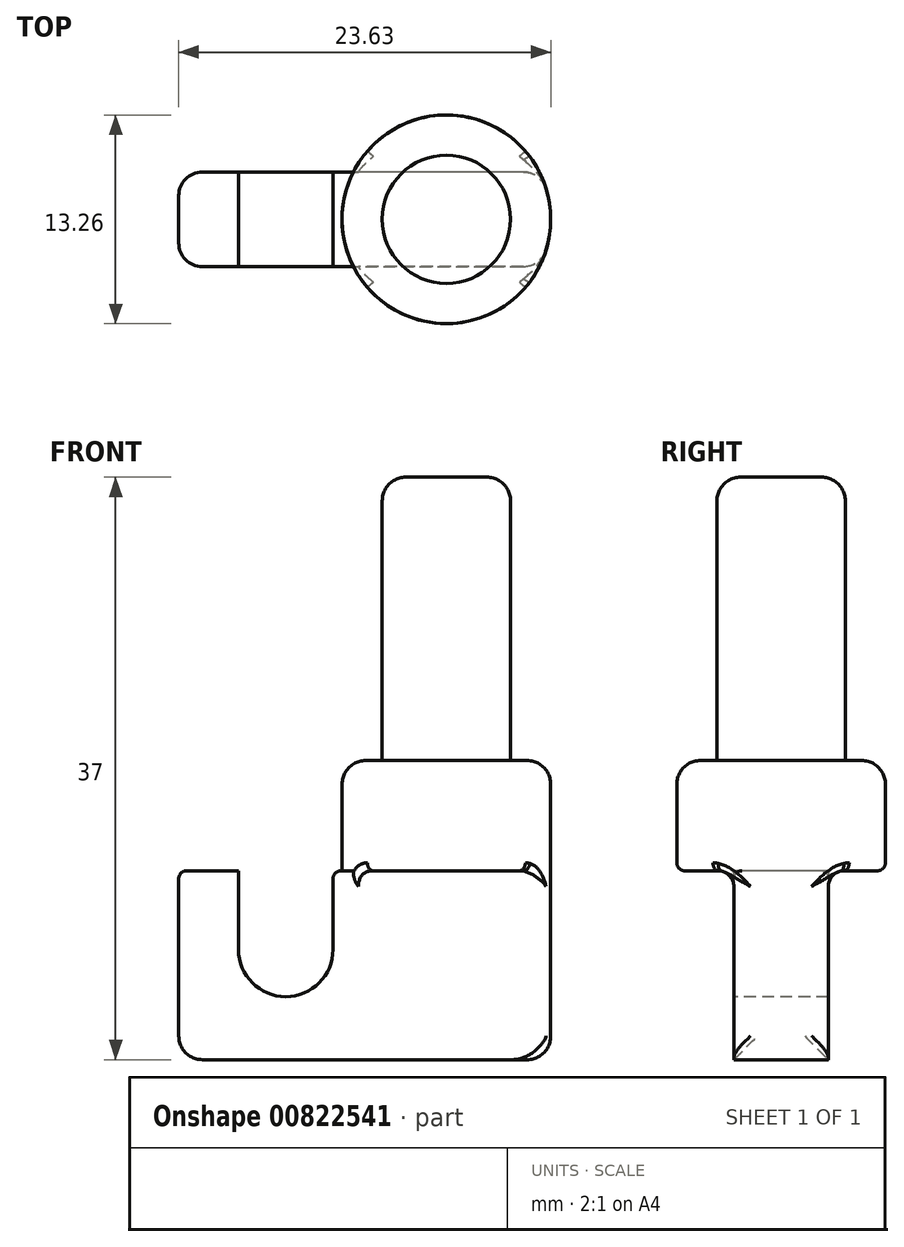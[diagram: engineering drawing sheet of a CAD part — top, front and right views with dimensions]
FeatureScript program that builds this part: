
annotation { "Feature Type Name" : "Feature", "Feature Type Description" : "" }
export const myFeature = defineFeature(function(context is Context, id is Id, definition is map)
    precondition{}
    {
        {
            var Q0;
            Q0=qCreatedBy(makeId("Top.planeOp"),FACE);
            var sketch = newSketch(context, id + "F0", { "sketchPlane" : qUnion([Q0])});
            skCircle(sketch, "E0", {"center": v(0, 0) * mm, "radius": 4.08 * mm});
            skCircle(sketch, "E1", {"center": v(0, 0) * mm, "radius": 6.62 * mm});
            skLineSegment(sketch, "E2", {"start": v(0, 0) * mm, "end": v(0, 3) * mm});
            skLineSegment(sketch, "E3", {"start": v(0, 3) * mm, "end": v(-17, 3) * mm});
            skLineSegment(sketch, "E4", {"start": v(-17, 3) * mm, "end": v(-17, -3) * mm});
            skLineSegment(sketch, "E5", {"start": v(-17, -3) * mm, "end": v(0, -3) * mm});
            skLineSegment(sketch, "E6", {"start": v(0, -3) * mm, "end": v(0, 0) * mm});
            skLineSegment(sketch, "E7", {"start": v(-6.62, 0) * mm, "end": v(-6.62, 3) * mm});
            skLineSegment(sketch, "E8", {"start": v(-6.63, 3) * mm, "end": v(-6.62, -3) * mm});
            skSolve(sketch);
        }
        {
            var Q0;
            {var subQ4=sQuery(id+"F0.wireOp",EDGE,"E2");Q0=makeQuery(id+"F0.imprint","IMPRINT",FACE,{"disambiguationData":[TD([[makeQuery(id+"F0.imprint","IMPRINT",EDGE,{"derivedFrom":subQ4}),-1.0]])]});}
            var Q1;
            {var subQ5=sQuery(id+"F0.wireOp",EDGE,"E2");Q1=makeQuery(id+"F0.imprint","IMPRINT",FACE,{"disambiguationData":[TD([[makeQuery(id+"F0.imprint","IMPRINT",EDGE,{"derivedFrom":subQ5}),1.0]])]});}
            extrude(context, id + "F1", {"entities" : qUnion([Q0, Q1]), "depth" : 37 * mm, "offsetDistance" : 25 * mm});
        }
        {
            var Q0;
            {var subQ0=sQuery(id+"F0.wireOp",EDGE,"E3");var subQ1=sQuery(id+"F0.wireOp",EDGE,"E0");var subQ2=makeQuery(id+"F0.imprint","INTERSECT",VERTEX,{"derivedFrom":[subQ1,subQ0]});Q0=makeQuery(id+"F0.imprint","IMPRINT",FACE,{"disambiguationData":[TD([[makeQuery(id+"F0.imprint","IMPRINT",EDGE,{"disambiguationData":[TD([[subQ2,1.0]])],"derivedFrom":subQ1}),-1.0]])]});}
            var Q1;
            {var subQ4=sQuery(id+"F0.wireOp",EDGE,"E3");var subQ6=sQuery(id+"F0.wireOp",EDGE,"E0");var subQ7=makeQuery(id+"F0.imprint","INTERSECT",VERTEX,{"derivedFrom":[subQ6,subQ4]});Q1=makeQuery(id+"F0.imprint","IMPRINT",FACE,{"disambiguationData":[TD([[makeQuery(id+"F0.imprint","IMPRINT",EDGE,{"disambiguationData":[TD([[subQ7,-1.0]])],"derivedFrom":subQ6}),-1.0]])]});}
            extrude(context, id + "F2", {"entities" : qUnion([Q0, Q1]), "operationType" : NewBodyOperationType.ADD, "depth" : 19 * mm, "offsetDistance" : 25 * mm});
        }
        {
            var Q0;
            {var subQ0=sQuery(id+"F0.wireOp",EDGE,"E3");var subQ1=sQuery(id+"F0.wireOp",EDGE,"E1");var subQ2=makeQuery(id+"F0.imprint","INTERSECT",VERTEX,{"derivedFrom":[subQ1,subQ0]});Q0=makeQuery(id+"F0.imprint","IMPRINT",FACE,{"disambiguationData":[TD([[makeQuery(id+"F0.imprint","IMPRINT",EDGE,{"disambiguationData":[TD([[subQ2,-1.0]])],"derivedFrom":subQ1}),-1.0]])]});}
            var Q1;
            {var subQ0=sQuery(id+"F0.wireOp",EDGE,"E5");var subQ1=sQuery(id+"F0.wireOp",EDGE,"E1");var subQ2=makeQuery(id+"F0.imprint","INTERSECT",VERTEX,{"derivedFrom":[subQ1,subQ0]});Q1=makeQuery(id+"F0.imprint","IMPRINT",FACE,{"disambiguationData":[TD([[makeQuery(id+"F0.imprint","IMPRINT",EDGE,{"disambiguationData":[TD([[subQ2,1.0]])],"derivedFrom":subQ1}),-1.0]])]});}
            var Q2;
            {var subQ5=sQuery(id+"F0.wireOp",EDGE,"E4");Q2=makeQuery(id+"F0.imprint","IMPRINT",FACE,{"disambiguationData":[TD([[makeQuery(id+"F0.imprint","IMPRINT",EDGE,{"derivedFrom":subQ5}),1.0]])]});}
            extrude(context, id + "F3", {"entities" : qUnion([Q0, Q1, Q2]), "operationType" : NewBodyOperationType.ADD, "depth" : 12 * mm, "offsetDistance" : 25 * mm});
        }
        {
            var Q0;
            Q0=makeQuery(id+"F3.opExtrude","SWEPT_FACE",FACE,{"disambiguationData":[OSD([sQuery(id+"F0.wireOp",EDGE,"E4")])]});
            var sketch = newSketch(context, id + "F4", { "sketchPlane" : qUnion([Q0])});
            skLineSegment(sketch, "E9", {"start": v(-3, 12) * mm, "end": v(-7.58, 12) * mm});
            skLineSegment(sketch, "E10", {"start": v(-7.58, 12) * mm, "end": v(-7.58, 0) * mm});
            skLineSegment(sketch, "E11", {"start": v(-7.58, 0) * mm, "end": v(10.46, 0) * mm});
            skLineSegment(sketch, "E12", {"start": v(10.46, 0) * mm, "end": v(10.46, 12) * mm});
            skLineSegment(sketch, "E13", {"start": v(10.46, 12) * mm, "end": v(3, 12) * mm});
            skSolve(sketch);
        }
        {
            var Q0;
            Q0=makeQuery(id+"F4.imprint","IMPRINT",FACE,{"disambiguationData":[TD([[makeQuery(id+"F4.imprint","IMPRINT",EDGE,{"derivedFrom":sQuery(id+"F4.wireOp",EDGE,"E9")}),1.0]])]});
            var Q1;
            {var subQ2=sQuery(id+"F4.wireOp",EDGE,"E12");Q1=makeQuery(id+"F4.imprint","IMPRINT",FACE,{"disambiguationData":[TD([[makeQuery(id+"F4.imprint","IMPRINT",EDGE,{"derivedFrom":subQ2}),1.0]])]});}
            extrude(context, id + "F5", {"entities" : qUnion([Q0, Q1]), "operationType" : NewBodyOperationType.REMOVE, "oppositeDirection" : true, "depth" : 25 * mm, "offsetDistance" : 25 * mm});
        }
        {
            var Q0;
            Q0=makeQuery(id+"F3.opExtrude","SWEPT_EDGE",EDGE,{"disambiguationData":[OSD([sQuery(id+"F0.wireOp",EDGE,"E3"),sQuery(id+"F0.wireOp",EDGE,"E4")])]});
            var Q1;
            Q1=makeQuery(id+"F5.boolean.opBoolean","INTERSECT",EDGE,{"derivedFrom":[makeQuery(id+"F2.opExtrude","SWEPT_FACE",FACE,{"disambiguationData":[OSD([sQuery(id+"F0.wireOp",EDGE,"E1")])]}),makeQuery(id+"F5.opExtrude","SWEPT_FACE",FACE,{"disambiguationData":[OSD([sQuery(id+"F0.wireOp",EDGE,"E3"),sQuery(id+"F0.wireOp",EDGE,"E4")])]})]});
            var Q2;
            Q2=makeQuery(id+"F5.boolean.opBoolean","INTERSECT",EDGE,{"derivedFrom":[makeQuery(id+"F2.opExtrude","SWEPT_FACE",FACE,{"disambiguationData":[OSD([sQuery(id+"F0.wireOp",EDGE,"E1")])]}),makeQuery(id+"F5.opExtrude","SWEPT_FACE",FACE,{"disambiguationData":[OSD([sQuery(id+"F0.wireOp",EDGE,"E4"),sQuery(id+"F0.wireOp",EDGE,"E5")])]})]});
            var Q3;
            {var subQ0=sQuery(id+"F0.wireOp",EDGE,"E3");Q3=makeQuery(id+"F5.boolean.opBoolean","MERGE",EDGE,{"derivedFrom":[makeQuery(id+"F3.opExtrude","CAP_EDGE",EDGE,{"disambiguationData":[OSD([subQ0])],"isStart":true}),makeQuery(id+"F5.opExtrude","SWEPT_EDGE",EDGE,{"disambiguationData":[OSD([subQ0,sQuery(id+"F0.wireOp",EDGE,"E4"),sQuery(id+"F4.wireOp",EDGE,"E11")])]})]});}
            var Q4;
            {var subQ0=sQuery(id+"F0.wireOp",EDGE,"E5");Q4=makeQuery(id+"F5.boolean.opBoolean","MERGE",EDGE,{"derivedFrom":[makeQuery(id+"F3.opExtrude","CAP_EDGE",EDGE,{"disambiguationData":[OSD([subQ0])],"isStart":true}),makeQuery(id+"F5.opExtrude","SWEPT_EDGE",EDGE,{"disambiguationData":[OSD([sQuery(id+"F0.wireOp",EDGE,"E4"),subQ0,sQuery(id+"F4.wireOp",EDGE,"E11")])]})]});}
            var Q5;
            Q5=makeQuery(id+"F3.opExtrude","SWEPT_EDGE",EDGE,{"disambiguationData":[OSD([sQuery(id+"F0.wireOp",EDGE,"E4"),sQuery(id+"F0.wireOp",EDGE,"E5")])]});
            var Q6;
            Q6=makeQuery(id+"F2.opExtrude","CAP_EDGE",EDGE,{"disambiguationData":[OSD([sQuery(id+"F0.wireOp",EDGE,"E1")])],"isStart":false});
            var Q7;
            Q7=makeQuery(id+"F1.opExtrude","CAP_EDGE",EDGE,{"disambiguationData":[OSD([sQuery(id+"F0.wireOp",EDGE,"E0")])],"isStart":false});
            var Q8;
            Q8=makeQuery(id+"F3.opExtrude","CAP_EDGE",EDGE,{"disambiguationData":[OSD([sQuery(id+"F0.wireOp",EDGE,"E4")])],"isStart":true});
            var Q9;
            Q9=makeQuery(id+"F2.opExtrude","CAP_EDGE",EDGE,{"disambiguationData":[OSD([sQuery(id+"F0.wireOp",EDGE,"E1")])],"isStart":true});
            fillet(context, id + "F6", {"entities" : qUnion([Q0, Q1, Q2, Q3, Q4, Q5, Q6, Q7, Q8, Q9]), "radius" : 1.5 * mm, "tangentPropagation" : true, "allowEdgeOverflow" : false});
        }
        {
            var Q0;
            {var subQ0=sQuery(id+"F0.wireOp",EDGE,"E5");Q0=makeQuery(id+"F5.boolean.opBoolean","MERGE",FACE,{"derivedFrom":[makeQuery(id+"F3.opExtrude","SWEPT_FACE",FACE,{"disambiguationData":[OSD([subQ0])]}),makeQuery(id+"F5.opExtrude","SWEPT_FACE",FACE,{"disambiguationData":[OSD([sQuery(id+"F0.wireOp",EDGE,"E4"),subQ0])]})]});}
            var sketch = newSketch(context, id + "F7", { "sketchPlane" : qUnion([Q0])});
            skLineSegment(sketch, "E14", {"start": v(-13.2, 12) * mm, "end": v(-13.2, 7) * mm});
            skLineSegment(sketch, "E15", {"start": v(-13.2, 7) * mm, "end": v(-7.2, 7) * mm});
            skLineSegment(sketch, "E16", {"start": v(-7.2, 7) * mm, "end": v(-7.2, 12) * mm});
            skCircle(sketch, "E17", {"center": v(-10.2, 7) * mm, "radius": 3 * mm});
            skSolve(sketch);
        }
        {
            var Q0;
            {var subQ0=sQuery(id+"F7.wireOp",EDGE,"E15");Q0=makeQuery(id+"F7.imprint","IMPRINT",FACE,{"disambiguationData":[TD([[makeQuery(id+"F7.imprint","IMPRINT",EDGE,{"derivedFrom":subQ0}),-1.0]])]});}
            var Q1;
            {var subQ0=sQuery(id+"F7.wireOp",EDGE,"E14");Q1=makeQuery(id+"F7.imprint","IMPRINT",FACE,{"disambiguationData":[TD([[makeQuery(id+"F7.imprint","IMPRINT",EDGE,{"derivedFrom":subQ0}),1.0]])]});}
            var Q2;
            {var subQ0=sQuery(id+"F7.wireOp",EDGE,"E15");Q2=makeQuery(id+"F7.imprint","IMPRINT",FACE,{"disambiguationData":[TD([[makeQuery(id+"F7.imprint","IMPRINT",EDGE,{"derivedFrom":subQ0}),1.0]])]});}
            extrude(context, id + "F8", {"entities" : qUnion([Q0, Q1, Q2]), "operationType" : NewBodyOperationType.REMOVE, "endBound" : BoundingType.UP_TO_NEXT, "oppositeDirection" : true, "depth" : 25 * mm, "offsetDistance" : 25 * mm});
        }
        {
            var Q0;
            Q0=makeQuery(id+"F5.boolean.opBoolean","COPY",EDGE,{"derivedFrom":makeQuery(id+"F5.opExtrude","SWEPT_EDGE",EDGE,{"disambiguationData":[OSD([sQuery(id+"F0.wireOp",EDGE,"E3"),sQuery(id+"F0.wireOp",EDGE,"E4"),sQuery(id+"F4.wireOp",EDGE,"E9")])]})});
            var Q1;
            Q1=makeQuery(id+"F5.boolean.opBoolean","COPY",EDGE,{"derivedFrom":makeQuery(id+"F5.opExtrude","SWEPT_EDGE",EDGE,{"disambiguationData":[OSD([sQuery(id+"F0.wireOp",EDGE,"E4"),sQuery(id+"F0.wireOp",EDGE,"E5"),sQuery(id+"F4.wireOp",EDGE,"E13")])]})});
            var Q2;
            Q2=makeQuery(id+"F2.opExtrude","CAP_EDGE",EDGE,{"disambiguationData":[OSD([sQuery(id+"F0.wireOp",EDGE,"E0")])],"isStart":false});
            fillet(context, id + "F9", {"entities" : qUnion([Q0, Q1, Q2]), "radius" : 1 * mm, "tangentPropagation" : true, "allowEdgeOverflow" : false});
        }
        {
            var Q0;
            {var subQ0=sQuery(id+"F0.wireOp",EDGE,"E5");Q0=makeQuery(id+"F8.boolean.opBoolean","SPLIT",EDGE,{"disambiguationData":[TD([makeQuery(id+"F8.opExtrude","SWEPT_FACE",FACE,{"disambiguationData":[OSD([sQuery(id+"F7.wireOp",EDGE,"E14")])]})])],"derivedFrom":makeQuery(id+"F3.opExtrude","CAP_EDGE",EDGE,{"disambiguationData":[OSD([subQ0])],"isStart":false})});}
            var Q1;
            Q1=makeQuery(id+"F8.boolean.opBoolean","COPY",EDGE,{"derivedFrom":makeQuery(id+"F8.opExtrude","SWEPT_EDGE",EDGE,{"disambiguationData":[OSD([sQuery(id+"F0.wireOp",EDGE,"E5"),sQuery(id+"F7.wireOp",EDGE,"E14")])]})});
            var Q2;
            Q2=makeQuery(id+"F8.boolean.opBoolean","COPY",EDGE,{"derivedFrom":makeQuery(id+"F8.opExtrude","SWEPT_EDGE",EDGE,{"disambiguationData":[OSD([sQuery(id+"F0.wireOp",EDGE,"E5"),sQuery(id+"F7.wireOp",EDGE,"E16")])]})});
            var Q3;
            Q3=makeQuery(id+"F8.boolean.opBoolean","COPY",EDGE,{"derivedFrom":makeQuery(id+"F8.opExtrude","CAP_EDGE",EDGE,{"disambiguationData":[OSD([sQuery(id+"F7.wireOp",EDGE,"E16")])],"isStart":true})});
            var Q4;
            Q4=makeQuery(id+"F8.boolean.opBoolean","COPY",EDGE,{"derivedFrom":makeQuery(id+"F8.opExtrude","CAP_EDGE",EDGE,{"disambiguationData":[OSD([sQuery(id+"F7.wireOp",EDGE,"E16")])],"isStart":false})});
            var Q5;
            Q5=makeQuery(id+"F5.boolean.opBoolean","INTERSECT",EDGE,{"derivedFrom":[makeQuery(id+"F2.opExtrude","SWEPT_FACE",FACE,{"disambiguationData":[OSD([sQuery(id+"F0.wireOp",EDGE,"E1")])]}),makeQuery(id+"F5.opExtrude","SWEPT_FACE",FACE,{"disambiguationData":[OSD([sQuery(id+"F4.wireOp",EDGE,"E9")])]})]});
            var Q6;
            Q6=makeQuery(id+"F5.boolean.opBoolean","INTERSECT",EDGE,{"derivedFrom":[makeQuery(id+"F2.opExtrude","SWEPT_FACE",FACE,{"disambiguationData":[OSD([sQuery(id+"F0.wireOp",EDGE,"E1")])]}),makeQuery(id+"F5.opExtrude","SWEPT_FACE",FACE,{"disambiguationData":[OSD([sQuery(id+"F4.wireOp",EDGE,"E13")])]})]});
            fillet(context, id + "F10", {"entities" : qUnion([Q0, Q1, Q2, Q3, Q4, Q5, Q6]), "radius" : .5 * mm, "tangentPropagation" : true, "allowEdgeOverflow" : false});
        }
    });
